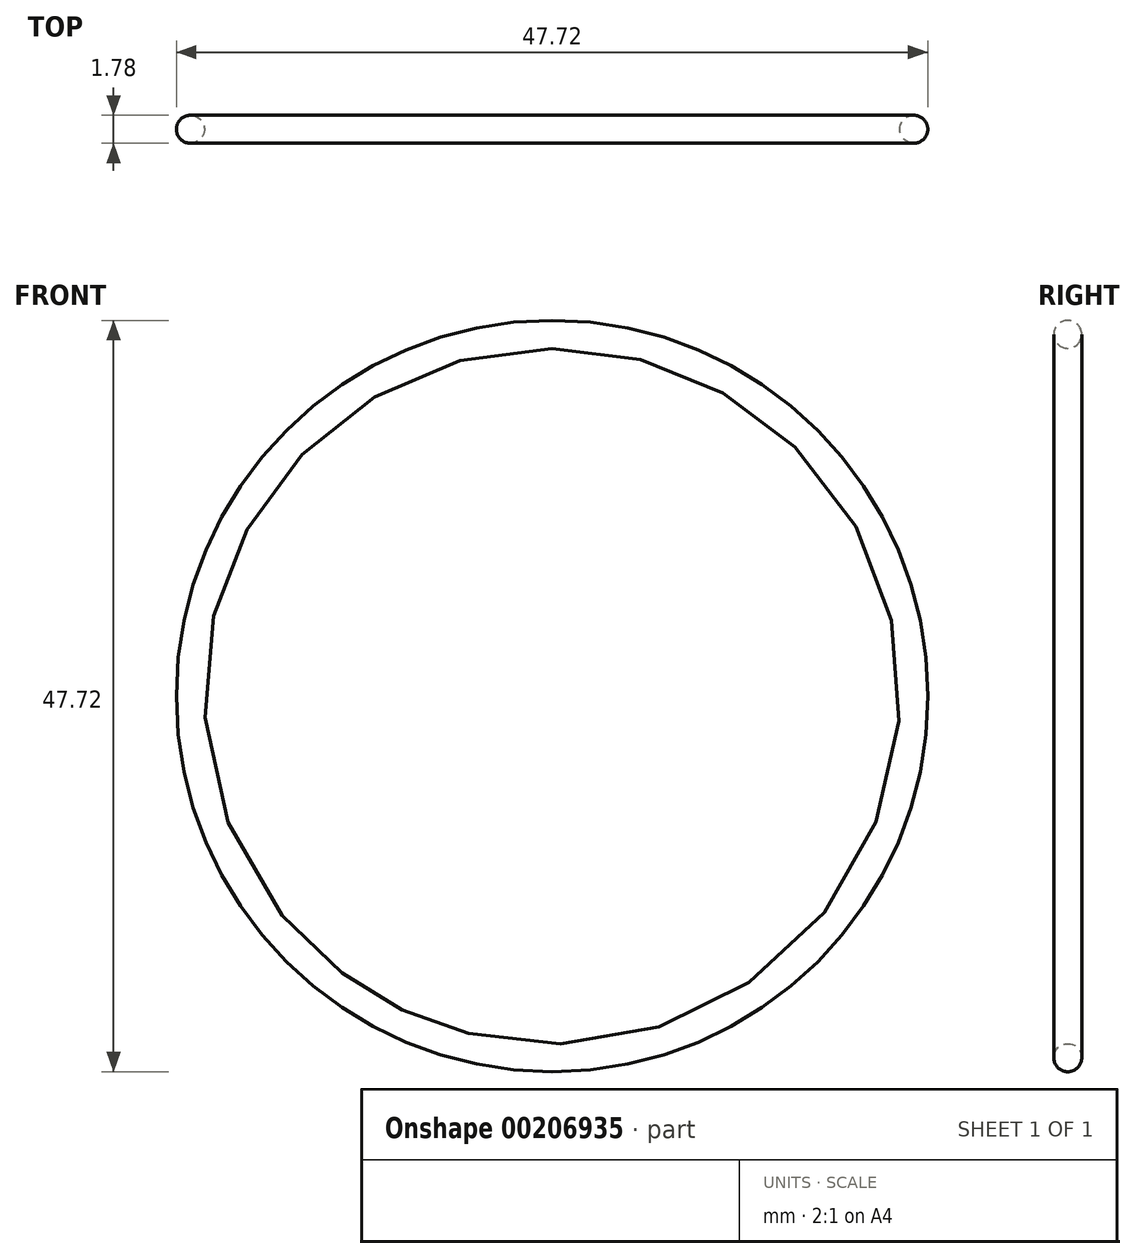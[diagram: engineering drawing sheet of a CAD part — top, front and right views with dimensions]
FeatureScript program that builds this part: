
annotation { "Feature Type Name" : "Feature", "Feature Type Description" : "" }
export const myFeature = defineFeature(function(context is Context, id is Id, definition is map)
    precondition{}
    {
        {
            var Q0;
            Q0=qCreatedBy(makeId("Top.planeOp"),FACE);
            var sketch = newSketch(context, id + "F0", { "sketchPlane" : qUnion([Q0])});
            skCircle(sketch, "E0", {"center": v(22.97, 0) * mm, "radius": 0.89 * mm});
            skLineSegment(sketch, "E1", {"start": v(0, 17.2) * mm, "end": v(0, -21) * mm, "construction": true});
            skSolve(sketch);
        }
        {
            var Q0;
            Q0 = qSketchRegion(id + "F0", true);
            var Q1;
            Q1=sQuery(id+"F0.wireOp",EDGE,"E1");
            revolve(context, id + "F1", {"entities" : qUnion([Q0]), "axis" : qUnion([Q1]), "revolveType" : RevolveType.FULL});
        }
    });
